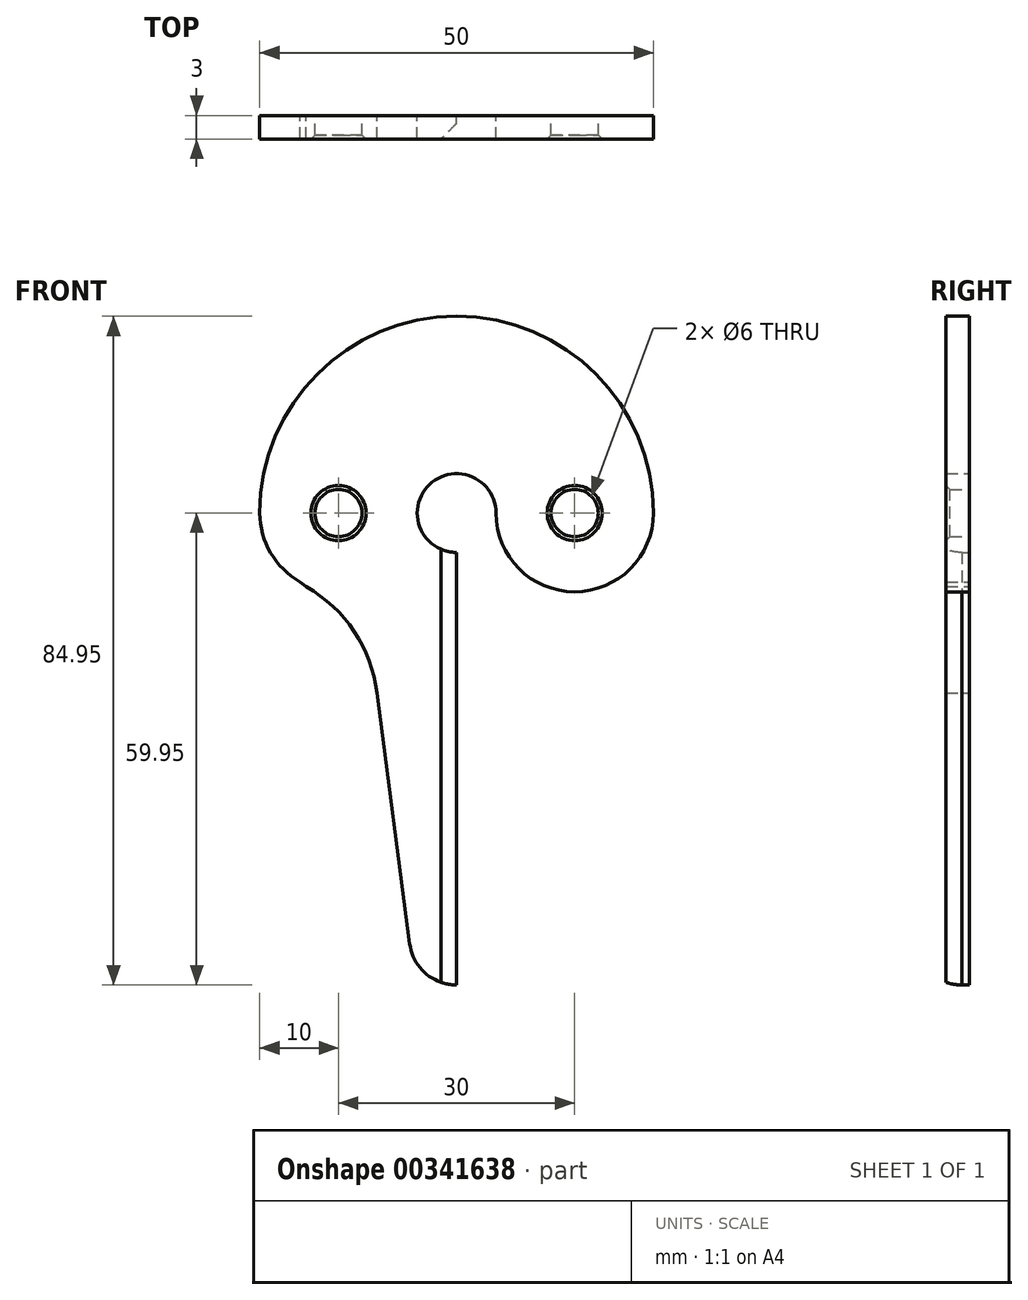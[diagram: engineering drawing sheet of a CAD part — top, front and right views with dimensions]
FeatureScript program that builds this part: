
annotation { "Feature Type Name" : "Feature", "Feature Type Description" : "" }
export const myFeature = defineFeature(function(context is Context, id is Id, definition is map)
    precondition{}
    {
        {
            var Q0;
            Q0=qCreatedBy(makeId("Front.planeOp"),FACE);
            var sketch = newSketch(context, id + "F0", { "sketchPlane" : qUnion([Q0])});
            skArc(sketch, "E0", {"start": v(25, 0) * mm, "mid": v(0, 25) * mm, "end": v(-25, 0) * mm});
            skCircle(sketch, "E1", {"center": v(15, 0) * mm, "radius": 3 * mm});
            skCircle(sketch, "E2", {"center": v(-15, 0) * mm, "radius": 3 * mm});
            skArc(sketch, "E3", {"start": v(5, 0) * mm, "mid": v(-3.54, 3.54) * mm, "end": v(0, -5) * mm});
            skLineSegment(sketch, "E4", {"start": v(0, -5) * mm, "end": v(0, -60) * mm});
            skPoint(sketch, "E5", {"position": v(-28, -25) * mm});
            skArc(sketch, "E6", {"start": v(5, 0) * mm, "mid": v(15, -10) * mm, "end": v(25, 0) * mm});
            skArc(sketch, "E7", {"start": v(-10.13, -22.86) * mm, "mid": v(-13, -15.04) * mm, "end": v(-19.1, -9.35) * mm});
            skArc(sketch, "E8", {"start": v(-5.95, -54.73) * mm, "mid": v(-3.96, -58.46) * mm, "end": v(0, -59.95) * mm});
            skLineSegment(sketch, "E9", {"start": v(-10.13, -22.86) * mm, "end": v(-5.95, -54.73) * mm});
            skArc(sketch, "E10", {"start": v(-25, 0) * mm, "mid": v(-23.63, -5.06) * mm, "end": v(-19.88, -8.73) * mm});
            skLineSegment(sketch, "E11", {"start": v(-19.88, -8.73) * mm, "end": v(-19.1, -9.35) * mm});
            skSolve(sketch);
        }
        {
            var Q0;
            Q0=makeQuery(id+"F0.imprint","IMPRINT",FACE,{"disambiguationData":[TD([[makeQuery(id+"F0.imprint","IMPRINT",EDGE,{"derivedFrom":sQuery(id+"F0.wireOp",EDGE,"E0")}),1.0]])]});
            extrude(context, id + "F1", {"entities" : qUnion([Q0]), "depth" : 3 * mm});
        }
        {
            var Q0;
            Q0=makeQuery(id+"F1.opExtrude","CAP_EDGE",EDGE,{"disambiguationData":[OSD([sQuery(id+"F0.wireOp",EDGE,"E2")])],"isStart":false});
            var Q1;
            Q1=makeQuery(id+"F1.opExtrude","CAP_EDGE",EDGE,{"disambiguationData":[OSD([sQuery(id+"F0.wireOp",EDGE,"E1")])],"isStart":false});
            chamfer(context, id + "F2", {"entities" : qUnion([Q0, Q1]), "width" : .5 * mm, "tangentPropagation" : true});
        }
        {
            var Q0;
            Q0=makeQuery(id+"F1.opExtrude","CAP_EDGE",EDGE,{"disambiguationData":[OSD([sQuery(id+"F0.wireOp",EDGE,"E4")])],"isStart":false});
            chamfer(context, id + "F3", {"entities" : qUnion([Q0]), "width" : 2 * mm, "tangentPropagation" : true});
        }
    });
